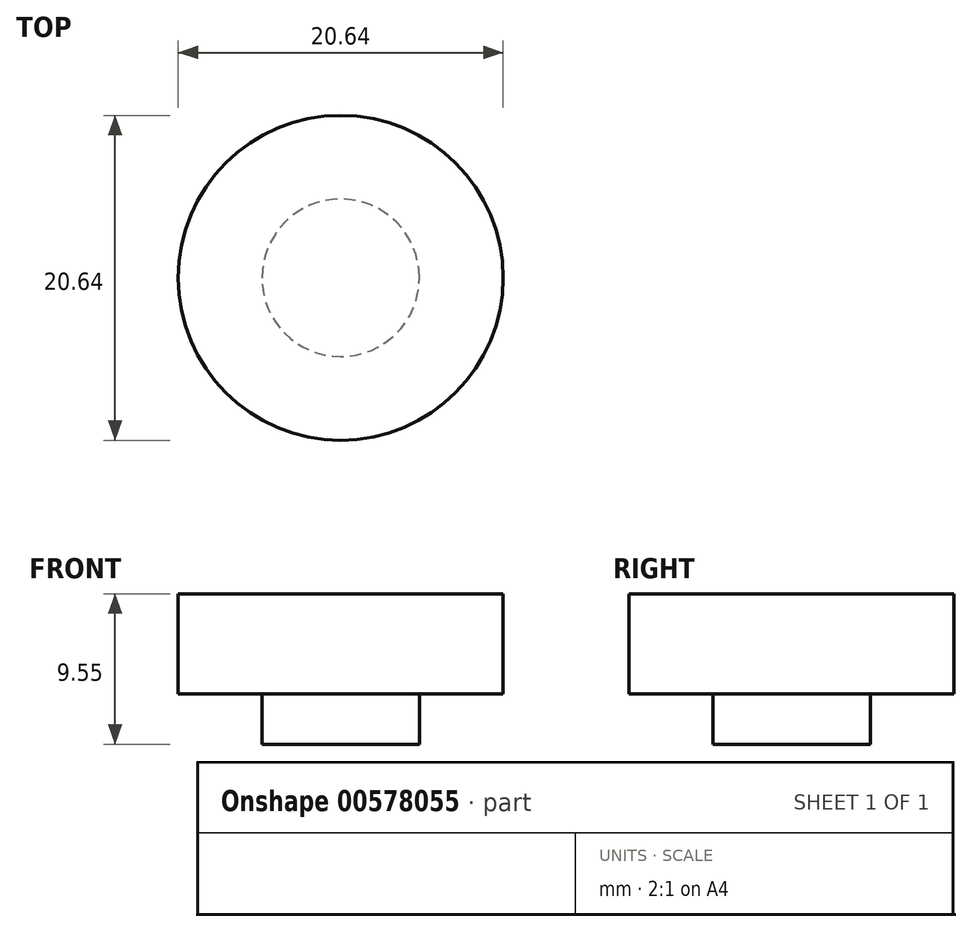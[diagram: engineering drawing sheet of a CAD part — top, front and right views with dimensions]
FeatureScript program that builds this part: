
annotation { "Feature Type Name" : "Feature", "Feature Type Description" : "" }
export const myFeature = defineFeature(function(context is Context, id is Id, definition is map)
    precondition{}
    {
        {
            var Q0;
            Q0=qCreatedBy(makeId("Top.planeOp"),FACE);
            var sketch = newSketch(context, id + "F0", { "sketchPlane" : qUnion([Q0])});
            skCircle(sketch, "E0", {"center": v(0, 0) * mm, "radius": 10.32 * mm});
            skSolve(sketch);
        }
        {
            var Q0;
            Q0=makeQuery(id+"F0.imprint","IMPRINT",FACE,{"disambiguationData":[TD([[makeQuery(id+"F0.imprint","IMPRINT",EDGE,{"derivedFrom":sQuery(id+"F0.wireOp",EDGE,"E0")}),1.0]])]});
            extrude(context, id + "F1", {"entities" : qUnion([Q0]), "depth" : 6.35 * mm, "offsetDistance" : 25.4 * mm});
        }
        {
            var Q0;
            Q0=makeQuery(id+"F1.opExtrude","CAP_FACE",FACE,{"disambiguationData":[OSD([sQuery(id+"F0.wireOp",EDGE,"E0")])],"isStart":true});
            var sketch = newSketch(context, id + "F2", { "sketchPlane" : qUnion([Q0])});
            skCircle(sketch, "E1", {"center": v(0, 0) * mm, "radius": 5 * mm});
            skSolve(sketch);
        }
        {
            var Q0;
            Q0=makeQuery(id+"F2.imprint","IMPRINT",FACE,{"disambiguationData":[TD([[makeQuery(id+"F2.imprint","IMPRINT",EDGE,{"derivedFrom":sQuery(id+"F2.wireOp",EDGE,"E1")}),1.0]])]});
            extrude(context, id + "F3", {"entities" : qUnion([Q0]), "operationType" : NewBodyOperationType.ADD, "depth" : 3.2 * mm, "offsetDistance" : 25.4 * mm});
        }
    });
